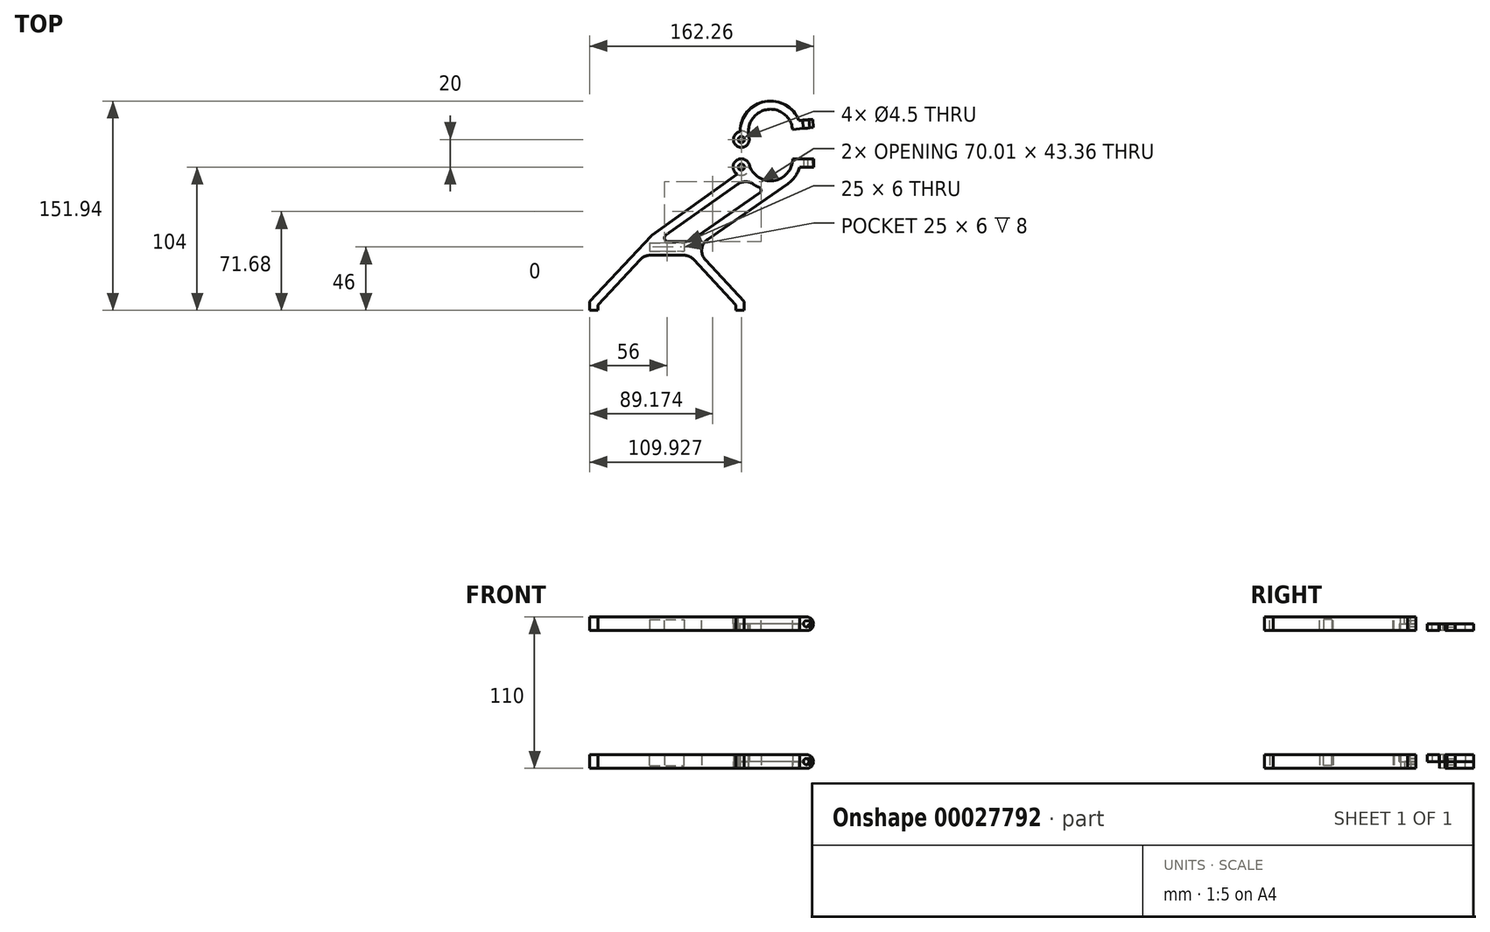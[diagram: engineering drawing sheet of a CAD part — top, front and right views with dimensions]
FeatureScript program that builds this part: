
annotation { "Feature Type Name" : "Feature", "Feature Type Description" : "" }
export const myFeature = defineFeature(function(context is Context, id is Id, definition is map)
    precondition{}
    {
        {
            var Q0;
            Q0=qCreatedBy(makeId("Top.planeOp"),FACE);
            var sketch = newSketch(context, id + "F0", { "sketchPlane" : qUnion([Q0])});
            skLineSegment(sketch, "E0", {"start": v(44.54, 54.16) * mm, "end": v(0, 6.36) * mm});
            skLineSegment(sketch, "E1", {"start": v(0, 6.36) * mm, "end": v(0, 0) * mm});
            skLineSegment(sketch, "E2", {"start": v(0, 0) * mm, "end": v(6, 0) * mm});
            skLineSegment(sketch, "E3", {"start": v(6, 0) * mm, "end": v(6, 4) * mm});
            skLineSegment(sketch, "E4", {"start": v(6, 4) * mm, "end": v(36.58, 36.82) * mm});
            skLineSegment(sketch, "E5", {"start": v(43.9, 40) * mm, "end": v(68.1, 40) * mm});
            skLineSegment(sketch, "E6", {"start": v(75.42, 36.82) * mm, "end": v(106, 4) * mm});
            skLineSegment(sketch, "E7", {"start": v(106, 4) * mm, "end": v(106, 0) * mm});
            skLineSegment(sketch, "E8", {"start": v(106, 0) * mm, "end": v(112, 0) * mm});
            skLineSegment(sketch, "E9", {"start": v(112, 0) * mm, "end": v(112, 6.36) * mm});
            skLineSegment(sketch, "E10", {"start": v(112, 6.36) * mm, "end": v(76, 45) * mm});
            skLineSegment(sketch, "E11", {"start": v(76, 45) * mm, "end": v(143.63, 91.92) * mm});
            skArc(sketch, "E12", {"start": v(109.93, 110) * mm, "mid": v(104.13, 105.55) * mm, "end": v(106.93, 98.8) * mm});
            skArc(sketch, "E13", {"start": v(115.7, 105.64) * mm, "mid": v(133.3, 94.15) * mm, "end": v(147.1, 110) * mm});
            skLineSegment(sketch, "E14", {"start": v(162.26, 110) * mm, "end": v(147.1, 110) * mm});
            skLineSegment(sketch, "E15", {"start": v(162.26, 104) * mm, "end": v(162.26, 110) * mm});
            skLineSegment(sketch, "E16", {"start": v(152.26, 104) * mm, "end": v(162.26, 104) * mm});
            skArc(sketch, "E17", {"start": v(143.63, 91.92) * mm, "mid": v(149, 97.21) * mm, "end": v(152.26, 104) * mm});
            skLineSegment(sketch, "E18", {"start": v(36, 45) * mm, "end": v(76, 45) * mm, "construction": true});
            skLineSegment(sketch, "E19", {"start": v(48.86, 50) * mm, "end": v(69.55, 50) * mm});
            skLineSegment(sketch, "E20", {"start": v(75.25, 51.78) * mm, "end": v(127.45, 88) * mm});
            skLineSegment(sketch, "E21", {"start": v(0, 0) * mm, "end": v(131.1, 110) * mm, "construction": true});
            skLineSegment(sketch, "E22", {"start": v(24.4, 32.54) * mm, "end": v(28.78, 28.45) * mm, "construction": true});
            skLineSegment(sketch, "E23", {"start": v(96.5, 23) * mm, "end": v(92.11, 18.9) * mm, "construction": true});
            skLineSegment(sketch, "E24", {"start": v(94.5, 65.14) * mm, "end": v(97.92, 60.21) * mm, "construction": true});
            skLineSegment(sketch, "E25", {"start": v(146.76, 106.78) * mm, "end": v(152.64, 105.57) * mm, "construction": true});
            skLineSegment(sketch, "E26", {"start": v(127.45, 88) * mm, "end": v(131.1, 88) * mm, "construction": true});
            skLineSegment(sketch, "E27", {"start": v(131.1, 88) * mm, "end": v(131.1, 94) * mm, "construction": true});
            skCircle(sketch, "E28", {"center": v(109.93, 104) * mm, "radius": 2.25 * mm});
            skLineSegment(sketch, "E29", {"start": v(109.93, 110) * mm, "end": v(109.93, 104) * mm, "construction": true});
            skLineSegment(sketch, "E30", {"start": v(106.93, 98.8) * mm, "end": v(109.93, 104) * mm, "construction": true});
            skPoint(sketch, "E31.visualSharp", {"position": v(36, 45) * mm});
            skPoint(sketch, "E32.visualSharp", {"position": v(39.54, 40) * mm});
            skArc(sketch, "E32.filletArc", {"start": v(43.9, 40) * mm, "mid": v(39.9, 39.17) * mm, "end": v(36.58, 36.82) * mm});
            skPoint(sketch, "E33.visualSharp", {"position": v(72.46, 40) * mm});
            skArc(sketch, "E33.filletArc", {"start": v(75.42, 36.82) * mm, "mid": v(72.1, 39.17) * mm, "end": v(68.1, 40) * mm});
            skPoint(sketch, "E34.visualSharp", {"position": v(72.68, 50) * mm});
            skArc(sketch, "E34.filletArc", {"start": v(69.55, 50) * mm, "mid": v(72.54, 50.46) * mm, "end": v(75.25, 51.78) * mm});
            skLineSegment(sketch, "E35", {"start": v(45.3, 54.83) * mm, "end": v(106.93, 98.8) * mm});
            skLineSegment(sketch, "E36", {"start": v(48.86, 50) * mm, "end": v(113.59, 96.19) * mm});
            skLineSegment(sketch, "E37", {"start": v(77.2, 77.6) * mm, "end": v(80.7, 72.71) * mm, "construction": true});
            skPoint(sketch, "E38", {"position": v(43.5, 49) * mm});
            skLineSegment(sketch, "E39", {"start": v(48.86, 50) * mm, "end": v(44.47, 54.1) * mm, "construction": true});
            skArc(sketch, "E40", {"start": v(113.59, 96.19) * mm, "mid": v(119.76, 90.8) * mm, "end": v(127.45, 88) * mm});
            skArc(sketch, "E41", {"start": v(115.7, 105.64) * mm, "mid": v(113.55, 108.79) * mm, "end": v(109.93, 110) * mm});
            skPoint(sketch, "E42.end.orphan", {"position": v(115.1, 110) * mm});
            skLineSegment(sketch, "E43", {"start": v(109.93, 110) * mm, "end": v(115.1, 110) * mm, "construction": true});
            skLineSegment(sketch, "E44", {"start": v(109.93, 104) * mm, "end": v(115.7, 105.64) * mm, "construction": true});
            skArc(sketch, "E45", {"start": v(118.48, 91.6) * mm, "mid": v(112.74, 93.36) * mm, "end": v(107.02, 91.5) * mm});
            skArc(sketch, "E46", {"start": v(85.49, 51.58) * mm, "mid": v(81.25, 44.44) * mm, "end": v(83.87, 36.55) * mm});
            skArc(sketch, "E47", {"start": v(55.22, 54.54) * mm, "mid": v(54.29, 51.74) * mm, "end": v(56.67, 50) * mm});
            skArc(sketch, "E48", {"start": v(123.12, 85) * mm, "mid": v(124.18, 87.32) * mm, "end": v(122.64, 89.36) * mm});
            skPoint(sketch, "E49.visualSharp", {"position": v(44.88, 54.53) * mm});
            skArc(sketch, "E49.filletArc", {"start": v(45.3, 54.83) * mm, "mid": v(44.9, 54.51) * mm, "end": v(44.54, 54.16) * mm});
            skSolve(sketch);
        }
        {
            var Q0;
            Q0 = qSketchRegion(id + "F0", true);
            var Q1;
            {var subQ0=sQuery(id+"F0.wireOp",EDGE,"E47");Q1=makeQuery(id+"F0.imprint","IMPRINT",FACE,{"disambiguationData":[TD([[makeQuery(id+"F0.imprint","IMPRINT",EDGE,{"derivedFrom":subQ0}),-1.0]])]});}
            var Q2;
            {var subQ0=sQuery(id+"F0.wireOp",EDGE,"E45");Q2=makeQuery(id+"F0.imprint","IMPRINT",FACE,{"disambiguationData":[TD([[makeQuery(id+"F0.imprint","IMPRINT",EDGE,{"derivedFrom":subQ0}),-1.0]])]});}
            var Q3;
            {var subQ0=sQuery(id+"F0.wireOp",EDGE,"E48");Q3=makeQuery(id+"F0.imprint","IMPRINT",FACE,{"disambiguationData":[TD([[makeQuery(id+"F0.imprint","IMPRINT",EDGE,{"derivedFrom":subQ0}),-1.0]])]});}
            extrude(context, id + "F1", {"entities" : qUnion([Q0, Q1, Q2, Q3]), "depth" : 10 * mm, "symmetric" : true});
        }
        {
            var Q0;
            Q0=makeQuery(id+"F1.opExtrude","SWEPT_FACE",FACE,{"disambiguationData":[OSD([sQuery(id+"F0.wireOp",EDGE,"E16")])]});
            var sketch = newSketch(context, id + "F2", { "sketchPlane" : qUnion([Q0])});
            skCircle(sketch, "E50", {"center": v(157.26, 0) * mm, "radius": 2.25 * mm});
            skArc(sketch, "E51", {"start": v(157.26, -5) * mm, "mid": v(162.26, 0) * mm, "end": v(157.26, 5) * mm});
            skLineSegment(sketch, "E52", {"start": v(157.26, -5) * mm, "end": v(162.26, -5) * mm});
            skLineSegment(sketch, "E53", {"start": v(162.26, -5) * mm, "end": v(162.26, 5) * mm});
            skLineSegment(sketch, "E54", {"start": v(162.26, 5) * mm, "end": v(157.26, 5) * mm});
            skSolve(sketch);
        }
        {
            var Q0;
            Q0 = qSketchRegion(id + "F2", true);
            extrude(context, id + "F3", {"entities" : qUnion([Q0]), "operationType" : NewBodyOperationType.REMOVE, "endBound" : BoundingType.THROUGH_ALL, "oppositeDirection" : true, "depth" : 25 * mm});
        }
        {
            var Q0;
            Q0=makeQuery(id+"F1.opExtrude","CAP_FACE",FACE,{"disambiguationData":[OSD([sQuery(id+"F0.wireOp",EDGE,"8654b762-f42e-4e54-a1a1-93a0492e9255"),sQuery(id+"F0.wireOp",EDGE,"E0"),sQuery(id+"F0.wireOp",EDGE,"E1"),sQuery(id+"F0.wireOp",EDGE,"E2"),sQuery(id+"F0.wireOp",EDGE,"E3"),sQuery(id+"F0.wireOp",EDGE,"E4"),sQuery(id+"F0.wireOp",EDGE,"E5"),sQuery(id+"F0.wireOp",EDGE,"E6"),sQuery(id+"F0.wireOp",EDGE,"E7"),sQuery(id+"F0.wireOp",EDGE,"E8"),sQuery(id+"F0.wireOp",EDGE,"E9"),sQuery(id+"F0.wireOp",EDGE,"E10"),sQuery(id+"F0.wireOp",EDGE,"E11"),sQuery(id+"F0.wireOp",EDGE,"E12"),sQuery(id+"F0.wireOp",EDGE,"E42"),sQuery(id+"F0.wireOp",EDGE,"E13"),sQuery(id+"F0.wireOp",EDGE,"E14"),sQuery(id+"F0.wireOp",EDGE,"E15"),sQuery(id+"F0.wireOp",EDGE,"E16"),sQuery(id+"F0.wireOp",EDGE,"E17"),sQuery(id+"F0.wireOp",EDGE,"E19"),sQuery(id+"F0.wireOp",EDGE,"E20"),sQuery(id+"F0.wireOp",EDGE,"3bac20cf-d173-4433-96f8-a9dfc64a6fbb"),sQuery(id+"F0.wireOp",EDGE,"0645d3f2-d8a1-47e1-a1c3-d69c6d73d3cb"),sQuery(id+"F0.wireOp",EDGE,"E28")])],"isStart":false});
            var sketch = newSketch(context, id + "F4", { "sketchPlane" : qUnion([Q0])});
            skLineSegment(sketch, "E55.bottom", {"start": v(43.5, 49) * mm, "end": v(68.5, 49) * mm});
            skLineSegment(sketch, "E55.top", {"start": v(43.5, 43) * mm, "end": v(68.5, 43) * mm});
            skLineSegment(sketch, "E55.left", {"start": v(43.5, 49) * mm, "end": v(43.5, 43) * mm});
            skLineSegment(sketch, "E55.right", {"start": v(68.5, 49) * mm, "end": v(68.5, 43) * mm});
            skPoint(sketch, "E56.0", {"position": v(43.5, 49) * mm});
            skSolve(sketch);
        }
        {
            var Q0;
            Q0 = qSketchRegion(id + "F4", true);
            extrude(context, id + "F5", {"entities" : qUnion([Q0]), "operationType" : NewBodyOperationType.REMOVE, "oppositeDirection" : true, "depth" : 8 * mm});
        }
        {
            var Q0;
            Q0=makeQuery(id+"F1.opExtrude","CAP_FACE",FACE,{"disambiguationData":[OSD([sQuery(id+"F0.wireOp",EDGE,"E0"),sQuery(id+"F0.wireOp",EDGE,"E1"),sQuery(id+"F0.wireOp",EDGE,"E2"),sQuery(id+"F0.wireOp",EDGE,"E3"),sQuery(id+"F0.wireOp",EDGE,"E4"),sQuery(id+"F0.wireOp",EDGE,"E5"),sQuery(id+"F0.wireOp",EDGE,"E6"),sQuery(id+"F0.wireOp",EDGE,"E7"),sQuery(id+"F0.wireOp",EDGE,"E8"),sQuery(id+"F0.wireOp",EDGE,"E9"),sQuery(id+"F0.wireOp",EDGE,"E10"),sQuery(id+"F0.wireOp",EDGE,"E11"),sQuery(id+"F0.wireOp",EDGE,"E12"),sQuery(id+"F0.wireOp",EDGE,"E13"),sQuery(id+"F0.wireOp",EDGE,"E14"),sQuery(id+"F0.wireOp",EDGE,"E15"),sQuery(id+"F0.wireOp",EDGE,"E16"),sQuery(id+"F0.wireOp",EDGE,"E17"),sQuery(id+"F0.wireOp",EDGE,"E19"),sQuery(id+"F0.wireOp",EDGE,"E20"),sQuery(id+"F0.wireOp",EDGE,"E28"),sQuery(id+"F0.wireOp",EDGE,"E32.filletArc"),sQuery(id+"F0.wireOp",EDGE,"E33.filletArc"),sQuery(id+"F0.wireOp",EDGE,"E34.filletArc"),sQuery(id+"F0.wireOp",EDGE,"E35"),sQuery(id+"F0.wireOp",EDGE,"E36"),sQuery(id+"F0.wireOp",EDGE,"E40"),sQuery(id+"F0.wireOp",EDGE,"E41")])],"isStart":false});
            var sketch = newSketch(context, id + "F6", { "sketchPlane" : qUnion([Q0])});
            skCircle(sketch, "E57", {"center": v(109.93, 104) * mm, "radius": 6 * mm});
            skSolve(sketch);
        }
        {
            var Q0;
            Q0 = qSketchRegion(id + "F6", true);
            extrude(context, id + "F7", {"entities" : qUnion([Q0]), "operationType" : NewBodyOperationType.REMOVE, "oppositeDirection" : true, "depth" : 5 * mm});
        }
        {
            var Q0;
            Q0=qCreatedBy(makeId("Top.planeOp"),FACE);
            var sketch = newSketch(context, id + "F8", { "sketchPlane" : qUnion([Q0])});
            skArc(sketch, "E58", {"start": v(147.05, 131.34) * mm, "mid": v(128.97, 145.8) * mm, "end": v(115.37, 127.08) * mm});
            skLineSegment(sketch, "E59", {"start": v(147.05, 131.34) * mm, "end": v(162.16, 132.66) * mm});
            skLineSegment(sketch, "E60", {"start": v(162.16, 132.66) * mm, "end": v(161.63, 138.64) * mm});
            skLineSegment(sketch, "E61", {"start": v(161.63, 138.64) * mm, "end": v(151.67, 137.77) * mm});
            skArc(sketch, "E62", {"start": v(151.67, 137.77) * mm, "mid": v(127, 151.56) * mm, "end": v(109.11, 129.7) * mm});
            skCircle(sketch, "E63", {"center": v(109.93, 124) * mm, "radius": 2.25 * mm});
            skCircle(sketch, "E64", {"center": v(109.93, 124) * mm, "radius": 6 * mm, "construction": true});
            skLineSegment(sketch, "E65", {"start": v(131.1, 129.94) * mm, "end": v(147.05, 131.34) * mm, "construction": true});
            skCircle(sketch, "E66.0", {"center": v(109.93, 124) * mm, "radius": 5.75 * mm});
            skLineSegment(sketch, "E67", {"start": v(109.93, 124) * mm, "end": v(115.7, 125.64) * mm, "construction": true});
            skLineSegment(sketch, "E68", {"start": v(131.1, 129.94) * mm, "end": v(115.1, 129.94) * mm, "construction": true});
            skCircle(sketch, "E69.0", {"center": v(109.93, 124) * mm, "radius": 6.25 * mm, "construction": true});
            skLineSegment(sketch, "E70", {"start": v(115.37, 127.08) * mm, "end": v(114.93, 126.83) * mm});
            skPoint(sketch, "E71", {"position": v(109.1, 129.94) * mm});
            skSolve(sketch);
        }
        {
            var Q0;
            Q0 = qSketchRegion(id + "F8", true);
            extrude(context, id + "F9", {"entities" : qUnion([Q0]), "operationType" : NewBodyOperationType.ADD, "depth" : 5 * mm});
        }
        {
            var Q0;
            Q0=makeQuery(id+"F9.opExtrude","SWEPT_BODY",BODY,{"disambiguationData":[OSD([sQuery(id+"F8.wireOp",EDGE,"E58"),sQuery(id+"F8.wireOp",EDGE,"E59"),sQuery(id+"F8.wireOp",EDGE,"E60"),sQuery(id+"F8.wireOp",EDGE,"E61"),sQuery(id+"F8.wireOp",EDGE,"E62"),sQuery(id+"F8.wireOp",EDGE,"E63"),sQuery(id+"F8.wireOp",EDGE,"E64"),sQuery(id+"F8.wireOp",EDGE,"140aa226-682f-464c-9869-2b3d8af1f9aa")])]});
            var Q1;
            Q1=qCreatedBy(makeId("Top.planeOp"),FACE);
            mirror(context, id + "F10", {"operationType" : NewBodyOperationType.ADD, "entities" : qUnion([Q0]), "mirrorPlane" : qUnion([Q1])});
        }
        {
            var Q0;
            Q0=makeQuery(id+"F10.opPattern","COPY",FACE,{"derivedFrom":makeQuery(id+"F9.opExtrude","CAP_FACE",FACE,{"disambiguationData":[OSD([sQuery(id+"F8.wireOp",EDGE,"E58"),sQuery(id+"F8.wireOp",EDGE,"E59"),sQuery(id+"F8.wireOp",EDGE,"E60"),sQuery(id+"F8.wireOp",EDGE,"E61"),sQuery(id+"F8.wireOp",EDGE,"E62"),sQuery(id+"F8.wireOp",EDGE,"E63"),sQuery(id+"F8.wireOp",EDGE,"E64"),sQuery(id+"F8.wireOp",EDGE,"d96c58fc-394f-4b6e-b8ca-a2715a05a401")])],"isStart":false}),"instanceName":"1"});
            var sketch = newSketch(context, id + "F11", { "sketchPlane" : qUnion([Q0])});
            skCircle(sketch, "E72", {"center": v(109.93, -124) * mm, "radius": 6.25 * mm});
            skSolve(sketch);
        }
        {
            var Q0;
            Q0 = qSketchRegion(id + "F11", true);
            extrude(context, id + "F12", {"entities" : qUnion([Q0]), "operationType" : NewBodyOperationType.REMOVE, "oppositeDirection" : true, "depth" : 5 * mm});
        }
        {
            var Q0;
            {var subQ0=makeQuery(id+"F9.opExtrude","SWEPT_FACE",FACE,{"disambiguationData":[OSD([sQuery(id+"F8.wireOp",EDGE,"E61")])]});Q0=makeQuery(id+"F10.boolean.opBoolean","MERGE",FACE,{"derivedFrom":[subQ0,makeQuery(id+"F10.opPattern","COPY",FACE,{"derivedFrom":subQ0,"instanceName":"1"})]});}
            var sketch = newSketch(context, id + "F13", { "sketchPlane" : qUnion([Q0])});
            skCircle(sketch, "E73", {"center": v(-168.1, 0) * mm, "radius": 2.25 * mm});
            skArc(sketch, "E74", {"start": v(-168.1, 5) * mm, "mid": v(-173.1, 0) * mm, "end": v(-168.1, -5) * mm});
            skLineSegment(sketch, "E75", {"start": v(-168.1, -5) * mm, "end": v(-173.1, -5) * mm});
            skLineSegment(sketch, "E76", {"start": v(-173.1, -5) * mm, "end": v(-173.1, 5) * mm});
            skLineSegment(sketch, "E77", {"start": v(-173.1, 5) * mm, "end": v(-168.1, 5) * mm});
            skSolve(sketch);
        }
        {
            var Q0;
            Q0 = qSketchRegion(id + "F13", true);
            extrude(context, id + "F14", {"entities" : qUnion([Q0]), "operationType" : NewBodyOperationType.REMOVE, "endBound" : BoundingType.THROUGH_ALL, "oppositeDirection" : true, "depth" : 25 * mm});
        }
        {
            var Q0;
            Q0=qCreatedBy(makeId("Top.planeOp"),FACE);
            cPlane(context, id + "F15", {"entities" : qUnion([Q0]), "cplaneType" : CPlaneType.OFFSET, "offset" : 50 * mm, "width" : 150 * mm, "height" : 150 * mm});
        }
        {
            var Q0;
            Q0=makeQuery(id+"F1.opExtrude","SWEPT_BODY",BODY,{"disambiguationData":[OSD([sQuery(id+"F0.wireOp",EDGE,"8654b762-f42e-4e54-a1a1-93a0492e9255"),sQuery(id+"F0.wireOp",EDGE,"E0"),sQuery(id+"F0.wireOp",EDGE,"E1"),sQuery(id+"F0.wireOp",EDGE,"E2"),sQuery(id+"F0.wireOp",EDGE,"E3"),sQuery(id+"F0.wireOp",EDGE,"E4"),sQuery(id+"F0.wireOp",EDGE,"E5"),sQuery(id+"F0.wireOp",EDGE,"E6"),sQuery(id+"F0.wireOp",EDGE,"E7"),sQuery(id+"F0.wireOp",EDGE,"E8"),sQuery(id+"F0.wireOp",EDGE,"E9"),sQuery(id+"F0.wireOp",EDGE,"E10"),sQuery(id+"F0.wireOp",EDGE,"E11"),sQuery(id+"F0.wireOp",EDGE,"E12"),sQuery(id+"F0.wireOp",EDGE,"E42"),sQuery(id+"F0.wireOp",EDGE,"E13"),sQuery(id+"F0.wireOp",EDGE,"E14"),sQuery(id+"F0.wireOp",EDGE,"E15"),sQuery(id+"F0.wireOp",EDGE,"E16"),sQuery(id+"F0.wireOp",EDGE,"E17"),sQuery(id+"F0.wireOp",EDGE,"E19"),sQuery(id+"F0.wireOp",EDGE,"E20"),sQuery(id+"F0.wireOp",EDGE,"3bac20cf-d173-4433-96f8-a9dfc64a6fbb"),sQuery(id+"F0.wireOp",EDGE,"0645d3f2-d8a1-47e1-a1c3-d69c6d73d3cb"),sQuery(id+"F0.wireOp",EDGE,"E28")])]});
            var Q1;
            Q1=qCreatedBy(id+"F15.planeOp",FACE);
            mirror(context, id + "F16", {"entities" : qUnion([Q0]), "mirrorPlane" : qUnion([Q1])});
        }
        {
            var Q0;
            Q0=makeQuery(id+"F9.opExtrude","SWEPT_BODY",BODY,{"disambiguationData":[OSD([sQuery(id+"F8.wireOp",EDGE,"E58"),sQuery(id+"F8.wireOp",EDGE,"E59"),sQuery(id+"F8.wireOp",EDGE,"E60"),sQuery(id+"F8.wireOp",EDGE,"E61"),sQuery(id+"F8.wireOp",EDGE,"E62"),sQuery(id+"F8.wireOp",EDGE,"E63"),sQuery(id+"F8.wireOp",EDGE,"E64"),sQuery(id+"F8.wireOp",EDGE,"140aa226-682f-464c-9869-2b3d8af1f9aa")])]});
            var Q1;
            Q1=qCreatedBy(id+"F15.planeOp",FACE);
            mirror(context, id + "F17", {"entities" : qUnion([Q0]), "mirrorPlane" : qUnion([Q1])});
        }
    });
